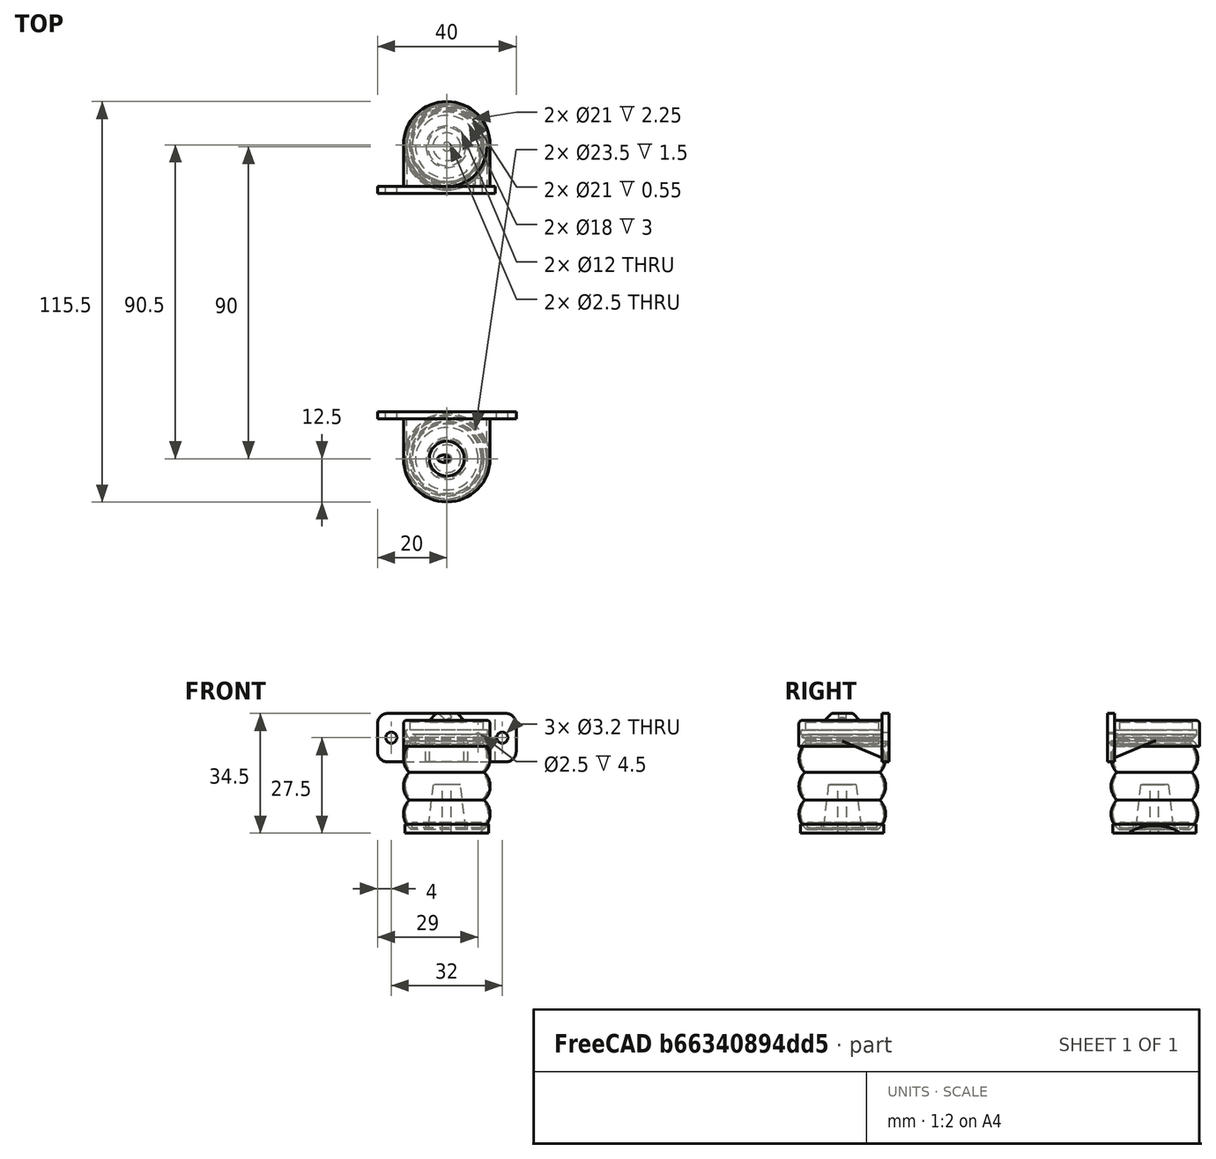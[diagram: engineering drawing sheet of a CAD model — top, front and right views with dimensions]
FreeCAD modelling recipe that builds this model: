
FCSTD DOCUMENT  (FreeCAD 0.16R)
Label: central-axle-lift-mech
License: All rights reserved
LicenseURL: http://en.wikipedia.org/wiki/All_rights_reserved
objects: Part::Cylinder×41, Part::Cut×32, Part::MultiFuse×24, Part::Torus×18, Part::Box×9, Part::Chamfer×7, Part::Fillet×5, Part::Cone×2, Part::Mirroring×1
note: 139 computed .brp shape members not serialized (recipe doc carries the construction recipe); baked Part::Feature solids carry a one-line shape summary decoded from their .brp

FEATURE [Part::Torus] Torus
  Angle1 = -180
  Angle2 = 180
  Angle3 = 360
  Placement = pos=(348.5,40,-30) rot=(0,0,1;0rad)
  Radius1 = 7
  Radius2 = 5.5
FEATURE [Part::Torus] Torus001
  Angle1 = -180
  Angle2 = 180
  Angle3 = 360
  Placement = pos=(348.5,40,-22) rot=(0,0,1;0rad)
  Radius1 = 7
  Radius2 = 5.5
FEATURE [Part::Torus] Torus002
  Angle1 = -180
  Angle2 = 180
  Angle3 = 360
  Placement = pos=(348.5,40,-14) rot=(0,0,1;0rad)
  Radius1 = 7
  Radius2 = 5.5
FEATURE [Part::Cylinder] Cylinder1050  label="Cylinder1207"
  Angle = 360
  Height = 5
  Placement = pos=(348.5,40,-12) rot=(0,0,1;0rad)
  Radius = 9
FEATURE [Part::Cylinder] Cylinder1051  label="Cylinder1208"
  Angle = 360
  Height = 1
  Placement = pos=(348.5,40,-35.5) rot=(0,0,1;0rad)
  Radius = 13
FEATURE [Part::Cylinder] Cylinder1053  label="Cylinder1209"
  Angle = 360
  Height = 1
  Placement = pos=(348.5,40,-8) rot=(0,0,1;0rad)
  Radius = 11.5
FEATURE [Part::Cylinder] Cylinder1054  label="Cylinder1210"
  Angle = 360
  Height = 3
  Placement = pos=(348.5,40,-10) rot=(0,0,1;0rad)
  Radius = 10.5
FEATURE [Part::Torus] Torus003
  Angle1 = -180
  Angle2 = 180
  Angle3 = 360
  Placement = pos=(348.5,40,-30) rot=(0,0,1;0rad)
  Radius1 = 7
  Radius2 = 5
FEATURE [Part::Torus] Torus004
  Angle1 = -180
  Angle2 = 180
  Angle3 = 360
  Placement = pos=(348.5,40,-22) rot=(0,0,1;0rad)
  Radius1 = 7
  Radius2 = 5
FEATURE [Part::Torus] Torus005
  Angle1 = -180
  Angle2 = 180
  Angle3 = 360
  Placement = pos=(348.5,40,-14) rot=(0,0,1;0rad)
  Radius1 = 7
  Radius2 = 5
FEATURE [Part::MultiFuse] Fusion704
  Shapes = -> [Torus,Torus001,Torus002]
FEATURE [Part::MultiFuse] Fusion705
  Shapes = -> [Torus003,Torus004,Torus005]
FEATURE [Part::Cylinder] Cylinder1056  label="Cylinder1211"
  Angle = 360
  Height = 2
  Placement = pos=(348.5,40,-34.5) rot=(0,0,1;0rad)
  Radius = 10
FEATURE [Part::Cylinder] Cylinder1057  label="Cylinder1212"
  Angle = 360
  Height = 36
  Placement = pos=(348.5,40,-34.5) rot=(0,0,1;0rad)
  Radius = 6
FEATURE [Part::Cut] Cut014209
  Base = -> Fusion704
  Tool = -> Fusion705
FEATURE [Part::MultiFuse] Fusion706
  Shapes = -> [Cut014209,Cylinder1054]
FEATURE [Part::Cut] Cut014210
  Base = -> Fusion706
  Tool = -> Cylinder1051
FEATURE [Part::MultiFuse] Fusion707
  Shapes = -> [Cylinder1053,Cut014210]
FEATURE [Part::Cut] Cut014211
  Base = -> Fusion707
  Tool = -> Cylinder1050
FEATURE [Part::MultiFuse] Fusion708
  Shapes = -> [Cut014211,Cylinder1056]
FEATURE [Part::Cut] Cut014212  label="central-axle-left-baloon"
  Base = -> Fusion708
  Tool = -> Cylinder1057
FEATURE [Part::Cylinder] Cylinder1065  label="Cylinder1213"
  Angle = 360
  Height = 6
  Placement = pos=(348.5,40,-9) rot=(0,0,1;0rad)
  Radius = 12.5
FEATURE [Part::Cylinder] Cylinder1066  label="Cylinder1214"
  Angle = 360
  Height = 3
  Placement = pos=(348.5,40,-10) rot=(0,0,1;0rad)
  Radius = 10.5
FEATURE [Part::Cylinder] Cylinder1067  label="Cylinder1215"
  Angle = 360
  Height = 1.5
  Placement = pos=(348.5,40,-8.25) rot=(0,0,1;0rad)
  Radius = 11.75
FEATURE [Part::MultiFuse] Fusion711
  Placement = pos=(0,0,1) rot=(0,0,1;0rad)
  Shapes = -> [Cylinder1067,Cylinder1066]
FEATURE [Part::Box] Box677  label="Cube868"
  Height = 6
  Length = 25
  Placement = pos=(336,40,-9) rot=(0,0,1;0rad)
  Width = 13.5
FEATURE [Part::Box] Box678  label="Cube869"
  Height = 14
  Length = 40
  Placement = pos=(328.5,51.5,-15) rot=(0,0,1;0rad)
  Width = 2
FEATURE [Part::Cylinder] Cylinder1068  label="Cylinder1216"
  Angle = 360
  Height = 6
  Placement = pos=(348.5,40,-15) rot=(0,0,1;0rad)
  Radius = 13
FEATURE [Part::Cylinder] Cylinder1069  label="Cylinder1217"
  Angle = 360
  Height = 5
  Placement = pos=(348.5,40,-8.5) rot=(0,0,1;0rad)
  Radius = 10.5
FEATURE [Part::Cylinder] Cylinder1070  label="Cylinder1218"
  Angle = 360
  Height = 12
  Placement = pos=(332.5,44,-8) rot=(-1,0,0;1.5708rad)
  Radius = 1.6
FEATURE [Part::Cylinder] Cylinder1071  label="Cylinder1219"
  Angle = 360
  Height = 12
  Placement = pos=(364.5,44,-8) rot=(-1,0,0;1.5708rad)
  Radius = 1.6
FEATURE [Part::MultiFuse] Fusion713
  Shapes = -> [Cylinder1071,Cylinder1070]
FEATURE [Part::Torus] Torus007
  Angle1 = -180
  Angle2 = 180
  Angle3 = 360
  Placement = pos=(348.5,40,-30) rot=(0,0,1;0rad)
  Radius1 = 7
  Radius2 = 5.5
FEATURE [Part::Cylinder] Cylinder1072  label="Cylinder1220"
  Angle = 360
  Height = 1
  Placement = pos=(348.5,40,-25.5) rot=(0,0,1;0rad)
  Radius = 13
FEATURE [Part::Cylinder] Cylinder1073  label="Cylinder1221"
  Angle = 360
  Height = 11
  Placement = pos=(348.5,40,-13.5) rot=(0,0,1;0rad)
  Radius = 8
FEATURE [Part::Cylinder] Cylinder1074  label="Cylinder1222"
  Angle = 360
  Height = 1.5
  Placement = pos=(348.5,40,-11.5) rot=(0,0,1;0rad)
  Radius = 12.5
FEATURE [Part::Cut] Cut014221
  Base = -> Torus007
  Placement = pos=(0,0,16) rot=(0,0,1;0rad)
  Tool = -> Cylinder1072
FEATURE [Part::Cut] Cut014222
  Base = -> Cylinder1074
  Tool = -> Cut014221
FEATURE [Part::Cut] Cut014223
  Base = -> Cut014222
  Placement = pos=(0,0,1) rot=(0,0,1;0rad)
  Tool = -> Cylinder1073
FEATURE [Part::Cylinder] Cylinder1075  label="Cylinder1223"
  Angle = 360
  Height = 2.5
  Placement = pos=(348.5,40,-12.5) rot=(0,0,1;0rad)
  Radius = 12.5
FEATURE [Part::Box] Box679  label="Cube870"
  Height = 5
  Length = 1
  Placement = pos=(336.5,40,-15) rot=(0,0,1;0rad)
  Width = 13.5
FEATURE [Part::Chamfer] Chamfer116
  Base = -> Box679
  Edges = 1 edges: [Edge9 r1=4.99 r2=12]
FEATURE [Part::Box] Box680  label="Cube871"
  Height = 5
  Length = 1
  Placement = pos=(336.5,40,-15) rot=(0,0,1;0rad)
  Width = 13.5
FEATURE [Part::Chamfer] Chamfer117
  Base = -> Box680
  Edges = 1 edges: [Edge9 r1=4.99 r2=12]
  Placement = pos=(24,0,0) rot=(0,0,1;0rad)
FEATURE [Part::MultiFuse] Fusion714
  Placement = pos=(-0.5,0,0) rot=(0,0,1;0rad)
  Shapes = -> [Chamfer116,Chamfer117]
FEATURE [Part::Cut] Cut014224
  Base = -> Fusion714
  Placement = pos=(0,0,1) rot=(0,0,1;0rad)
  Tool = -> Cylinder1075
FEATURE [Part::Torus] Torus008
  Angle1 = -180
  Angle2 = 180
  Angle3 = 360
  Placement = pos=(348.5,40,-30) rot=(0,0,1;0rad)
  Radius1 = 7
  Radius2 = 5.5
FEATURE [Part::Torus] Torus009
  Angle1 = -180
  Angle2 = 180
  Angle3 = 360
  Placement = pos=(348.5,40,-22) rot=(0,0,1;0rad)
  Radius1 = 7
  Radius2 = 5.5
FEATURE [Part::Torus] Torus010
  Angle1 = -180
  Angle2 = 180
  Angle3 = 360
  Placement = pos=(348.5,40,-14) rot=(0,0,1;0rad)
  Radius1 = 7
  Radius2 = 5.5
FEATURE [Part::Cylinder] Cylinder1076  label="Cylinder1224"
  Angle = 360
  Height = 5
  Placement = pos=(348.5,40,-12) rot=(0,0,1;0rad)
  Radius = 9
FEATURE [Part::Cylinder] Cylinder1077  label="Cylinder1225"
  Angle = 360
  Height = 1
  Placement = pos=(348.5,40,-35.5) rot=(0,0,1;0rad)
  Radius = 13
FEATURE [Part::Cylinder] Cylinder1078  label="Cylinder1226"
  Angle = 360
  Height = 1
  Placement = pos=(348.5,40,-8) rot=(0,0,1;0rad)
  Radius = 11.5
FEATURE [Part::Cylinder] Cylinder1079  label="Cylinder1227"
  Angle = 360
  Height = 3
  Placement = pos=(348.5,40,-10) rot=(0,0,1;0rad)
  Radius = 10.5
FEATURE [Part::Torus] Torus011
  Angle1 = -180
  Angle2 = 180
  Angle3 = 360
  Placement = pos=(348.5,40,-30) rot=(0,0,1;0rad)
  Radius1 = 7
  Radius2 = 5
FEATURE [Part::Torus] Torus012
  Angle1 = -180
  Angle2 = 180
  Angle3 = 360
  Placement = pos=(348.5,40,-22) rot=(0,0,1;0rad)
  Radius1 = 7
  Radius2 = 5
FEATURE [Part::Torus] Torus013
  Angle1 = -180
  Angle2 = 180
  Angle3 = 360
  Placement = pos=(348.5,40,-14) rot=(0,0,1;0rad)
  Radius1 = 7
  Radius2 = 5
FEATURE [Part::MultiFuse] Fusion716
  Shapes = -> [Torus008,Torus009,Torus010]
FEATURE [Part::MultiFuse] Fusion717
  Shapes = -> [Torus011,Torus012,Torus013]
FEATURE [Part::Cylinder] Cylinder1080  label="Cylinder1228"
  Angle = 360
  Height = 2
  Placement = pos=(348.5,40,-34.5) rot=(0,0,1;0rad)
  Radius = 10
FEATURE [Part::Cylinder] Cylinder1081  label="Cylinder1229"
  Angle = 360
  Height = 36
  Placement = pos=(348.5,40,-34.5) rot=(0,0,1;0rad)
  Radius = 6
FEATURE [Part::Cut] Cut014225
  Base = -> Fusion716
  Tool = -> Fusion717
FEATURE [Part::MultiFuse] Fusion718
  Shapes = -> [Cut014225,Cylinder1079]
FEATURE [Part::Cut] Cut014226
  Base = -> Fusion718
  Tool = -> Cylinder1077
FEATURE [Part::MultiFuse] Fusion719
  Shapes = -> [Cylinder1078,Cut014226]
FEATURE [Part::Cut] Cut014227
  Base = -> Fusion719
  Tool = -> Cylinder1076
FEATURE [Part::MultiFuse] Fusion720
  Shapes = -> [Cut014227,Cylinder1080]
FEATURE [Part::Cut] Cut014228  label="central-axle-right-baloon"
  Base = -> Fusion720
  Placement = pos=(0,90,0) rot=(0,0,1;0rad)
  Tool = -> Cylinder1081
FEATURE [Part::Cylinder] Cylinder1089  label="Cylinder1240"
  Angle = 360
  Height = 6
  Placement = pos=(348.5,130.5,-9) rot=(0,0,1;0rad)
  Radius = 12.5
FEATURE [Part::Cylinder] Cylinder1090  label="Cylinder1241"
  Angle = 360
  Height = 3
  Placement = pos=(348.5,40,-10) rot=(0,0,1;0rad)
  Radius = 10.5
FEATURE [Part::Cylinder] Cylinder1091  label="Cylinder1242"
  Angle = 360
  Height = 1.5
  Placement = pos=(348.5,40,-8.25) rot=(0,0,1;0rad)
  Radius = 11.75
FEATURE [Part::MultiFuse] Fusion723
  Placement = pos=(0,90.5,1) rot=(0,0,1;0rad)
  Shapes = -> [Cylinder1091,Cylinder1090]
FEATURE [Part::Box] Box682  label="Cube873"
  Height = 6
  Length = 25
  Placement = pos=(336,117,-9) rot=(0,0,1;0rad)
  Width = 13.5
FEATURE [Part::Box] Box683  label="Cube874"
  Height = 14
  Length = 34
  Placement = pos=(328.5,116.5,-15) rot=(0,0,1;0rad)
  Width = 2
FEATURE [Part::Cylinder] Cylinder1092  label="Cylinder1243"
  Angle = 360
  Height = 6
  Placement = pos=(348.5,130.5,-15) rot=(0,0,1;0rad)
  Radius = 13
FEATURE [Part::Cylinder] Cylinder1093  label="Cylinder1244"
  Angle = 360
  Height = 5
  Placement = pos=(348.5,130.5,-8.5) rot=(0,0,1;0rad)
  Radius = 10.5
FEATURE [Part::Cylinder] Cylinder1094  label="Cylinder1245"
  Angle = 360
  Height = 12
  Placement = pos=(332.5,109,-8) rot=(-1,0,0;1.5708rad)
  Radius = 1.6
FEATURE [Part::Torus] Torus015
  Angle1 = -180
  Angle2 = 180
  Angle3 = 360
  Placement = pos=(348.5,40,-30) rot=(0,0,1;0rad)
  Radius1 = 7
  Radius2 = 5.5
FEATURE [Part::Cylinder] Cylinder1096  label="Cylinder1247"
  Angle = 360
  Height = 1
  Placement = pos=(348.5,40,-25.5) rot=(0,0,1;0rad)
  Radius = 13
FEATURE [Part::Cylinder] Cylinder1097  label="Cylinder1248"
  Angle = 360
  Height = 11
  Placement = pos=(348.5,40,-13.5) rot=(0,0,1;0rad)
  Radius = 8
FEATURE [Part::Cylinder] Cylinder1098  label="Cylinder1249"
  Angle = 360
  Height = 1.5
  Placement = pos=(348.5,40,-11.5) rot=(0,0,1;0rad)
  Radius = 12.5
FEATURE [Part::Cut] Cut014238
  Base = -> Torus015
  Placement = pos=(0,0,16) rot=(0,0,1;0rad)
  Tool = -> Cylinder1096
FEATURE [Part::Cut] Cut014239
  Base = -> Cylinder1098
  Tool = -> Cut014238
FEATURE [Part::Cut] Cut014240
  Base = -> Cut014239
  Placement = pos=(0,90.5,1) rot=(0,0,1;0rad)
  Tool = -> Cylinder1097
FEATURE [Part::Cylinder] Cylinder1099  label="Cylinder1250"
  Angle = 360
  Height = 2.5
  Placement = pos=(348.5,40,-12.5) rot=(0,0,1;0rad)
  Radius = 12.5
FEATURE [Part::Box] Box684  label="Cube875"
  Height = 5
  Length = 1
  Placement = pos=(336.5,40,-15) rot=(0,0,1;0rad)
  Width = 13.5
FEATURE [Part::Chamfer] Chamfer118
  Base = -> Box684
  Edges = 1 edges: [Edge9 r1=4.99 r2=12]
FEATURE [Part::Box] Box685  label="Cube876"
  Height = 5
  Length = 1
  Placement = pos=(336.5,40,-15) rot=(0,0,1;0rad)
  Width = 13.5
FEATURE [Part::Chamfer] Chamfer119
  Base = -> Box685
  Edges = 1 edges: [Edge9 r1=4.99 r2=12]
  Placement = pos=(24,0,0) rot=(0,0,1;0rad)
FEATURE [Part::MultiFuse] Fusion726
  Placement = pos=(-0.5,0,0) rot=(0,0,1;0rad)
  Shapes = -> [Chamfer118,Chamfer119]
FEATURE [Part::Cut] Cut014241
  Base = -> Fusion726
  Tool = -> Cylinder1099
FEATURE [Part::Mirroring] Part__Mirroring093  label="Cut014241 (Mirror #11)"
  Base = (0,0,0)
  Normal = (0,1,0)
  Placement = pos=(0,170,1) rot=(0,0,1;0rad)
  Source = -> Cut014241
FEATURE [Part::Cylinder] Cylinder1100  label="Cylinder1251"
  Angle = 360
  Height = 12
  Placement = pos=(357.5,109,-8) rot=(-1,0,0;1.5708rad)
  Radius = 1.25
FEATURE [Part::MultiFuse] Fusion729
  Shapes = -> [Cylinder1094,Cylinder1100]
FEATURE [Part::MultiFuse] Fusion732
  Shapes = -> [Box682,Cylinder1089,Box683]
FEATURE [Part::Cut] Cut014250
  Base = -> Fusion732
  Tool = -> Fusion723
FEATURE [Part::Cut] Cut014251
  Base = -> Cut014250
  Tool = -> Cylinder1093
FEATURE [Part::Chamfer] Chamfer120
  Base = -> Cut014251
  Edges = 1 edges r=1.2: [Edge2]
FEATURE [Part::Cut] Cut014252
  Base = -> Chamfer120
  Tool = -> Cylinder1092
FEATURE [Part::MultiFuse] Fusion733
  Shapes = -> [Cut014240,Part__Mirroring093,Cut014252]
FEATURE [Part::Cut] Cut014253
  Base = -> Fusion733
  Tool = -> Fusion729
FEATURE [Part::Fillet] Fillet407
  Base = -> Cut014253
  Edges = 2 edges r=3: [Edge66,Edge69]
FEATURE [Part::Fillet] Fillet408  label="central-axle-right-baloon-upper-retainer_00"
  Base = -> Fillet407
  Edges = 1 edges r=1: [Edge57]
FEATURE [Part::MultiFuse] Fusion734
  Shapes = -> [Box677,Cylinder1065,Box678]
FEATURE [Part::Cut] Cut014254
  Base = -> Fusion734
  Tool = -> Fusion711
FEATURE [Part::Chamfer] Chamfer121
  Base = -> Cut014254
  Edges = 1 edges r=1.2: [Edge27]
FEATURE [Part::Cut] Cut014255
  Base = -> Chamfer121
  Tool = -> Cylinder1068
FEATURE [Part::Cut] Cut014256
  Base = -> Cut014255
  Tool = -> Cylinder1069
FEATURE [Part::Cut] Cut014257
  Base = -> Cut014256
  Tool = -> Fusion713
FEATURE [Part::Fillet] Fillet409
  Base = -> Cut014257
  Edges = 4 edges r=3: [Edge35,Edge36,Edge37,Edge40]
FEATURE [Part::Fillet] Fillet410
  Base = -> Fillet409
  Edges = 1 edges r=1: [Edge38]
FEATURE [Part::MultiFuse] Fusion735  label="central-axle-left-baloon-upper-retainer_00"
  Shapes = -> [Cut014223,Cut014224,Fillet410]
FEATURE [Part::Torus] Torus017
  Angle1 = -180
  Angle2 = 180
  Angle3 = 360
  Placement = pos=(348.5,40,-30) rot=(0,0,1;0rad)
  Radius1 = 7
  Radius2 = 5.5
FEATURE [Part::Cylinder] Cylinder1111  label="Cylinder1278"
  Angle = 360
  Height = 1
  Placement = pos=(348.5,40,-35.5) rot=(0,0,1;0rad)
  Radius = 13
FEATURE [Part::Cut] Cut014264
  Base = -> Torus017
  Tool = -> Cylinder1111
FEATURE [Part::Cylinder] Cylinder1112  label="Cylinder1279"
  Angle = 360
  Height = 2.5
  Placement = pos=(348.5,40,-35.5) rot=(0,0,1;0rad)
  Radius = 12
FEATURE [Part::Cut] Cut014265
  Base = -> Cylinder1112
  Tool = -> Cut014264
FEATURE [Part::Cylinder] Cylinder1115  label="Cylinder1282"
  Angle = 360
  Height = 14
  Placement = pos=(348.5,40,-35.5) rot=(0,0,1;0rad)
  Radius = 1.25
FEATURE [Part::Cone] Cone
  Angle = 360
  Height = 13
  Placement = pos=(348.5,40,-34.5) rot=(0,0,1;0rad)
  Radius1 = 5.5
  Radius2 = 4
FEATURE [Part::MultiFuse] Fusion739
  Shapes = -> [Cut014265,Cone]
FEATURE [Part::Cut] Cut014266  label="central-axle-left-baloon-plate"
  Base = -> Fusion739
  Tool = -> Cylinder1115
FEATURE [Part::Torus] Torus018
  Angle1 = -180
  Angle2 = 180
  Angle3 = 360
  Placement = pos=(348.5,40,-30) rot=(0,0,1;0rad)
  Radius1 = 7
  Radius2 = 5.5
FEATURE [Part::Cylinder] Cylinder1116  label="Cylinder1286"
  Angle = 360
  Height = 1
  Placement = pos=(348.5,40,-35.5) rot=(0,0,1;0rad)
  Radius = 13
FEATURE [Part::Cut] Cut014267
  Base = -> Torus018
  Tool = -> Cylinder1116
FEATURE [Part::Cylinder] Cylinder1117  label="Cylinder1287"
  Angle = 360
  Height = 2.5
  Placement = pos=(348.5,40,-35.5) rot=(0,0,1;0rad)
  Radius = 12
FEATURE [Part::Cut] Cut014268
  Base = -> Cylinder1117
  Tool = -> Cut014267
FEATURE [Part::Cylinder] Cylinder1118  label="Cylinder1288"
  Angle = 360
  Height = 14
  Placement = pos=(348.5,40,-35.5) rot=(0,0,1;0rad)
  Radius = 1.25
FEATURE [Part::Cone] Cone001
  Angle = 360
  Height = 13
  Placement = pos=(348.5,40,-34.5) rot=(0,0,1;0rad)
  Radius1 = 5.5
  Radius2 = 4
FEATURE [Part::MultiFuse] Fusion740
  Shapes = -> [Cut014268,Cone001]
FEATURE [Part::Cut] Cut014269
  Base = -> Fusion740
  Placement = pos=(0,90,0) rot=(0,0,1;0rad)
  Tool = -> Cylinder1118
FEATURE [Part::Box] Box690  label="Cube881"
  Height = 10
  Length = 10
  Placement = pos=(355.5,121,-37.5) rot=(0,1,0;0.872665rad)
  Width = 20
FEATURE [Part::Cut] Cut014270  label="central-axle-right-baloon-plate"
  Base = -> Cut014269
  Tool = -> Box690
FEATURE [Part::Cylinder] Cylinder1119
  Angle = 360
  Height = 2.5
  Placement = pos=(348.5,40,-3.5) rot=(0,0,1;0rad)
  Radius = 5
FEATURE [Part::Torus] Torus019
  Angle1 = -180
  Angle2 = 180
  Angle3 = 45
  Placement = pos=(344,40,-5) rot=(0.950615,-0.219467,0.219467;1.62142rad)
  Radius1 = 5.5
  Radius2 = 1.1
FEATURE [Part::Torus] Torus020
  Angle1 = -180
  Angle2 = 180
  Angle3 = 90
  Placement = pos=(344,40,-5) rot=(1,0,0;1.5708rad)
  Radius1 = 5.5
  Radius2 = 0.6
FEATURE [Part::MultiFuse] Fusion
  Shapes = -> [Torus020,Torus019]
FEATURE [Part::MultiFuse] Fusion741
  Shapes = -> [Cylinder1119,Fusion735]
FEATURE [Part::Cut] Cut
  Base = -> Fusion741
  Tool = -> Fusion
FEATURE [Part::Chamfer] Chamfer
  Base = -> Cut
  Edges = 1 edges r=1.99: [Edge1]
FEATURE [Part::Fillet] Fillet  label="central-axle-left-baloon-upper-retainer-with-lifter"
  Base = -> Chamfer
  Edges = 1 edges r=0.5: [Edge1]
